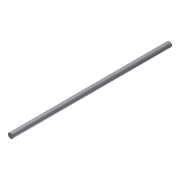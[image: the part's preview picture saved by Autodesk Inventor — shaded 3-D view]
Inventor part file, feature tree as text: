
AUTODESK INVENTOR PART (.ipt)
format: ipt  version: 2016 (Build 200138000, 138)  size: 82,432 bytes
history: native  units: in
note: dims shown in document units (in); Inventor stores cm internally (conversion verified against a paired STEP export)
features: other x1, imported_body x1, extrude x1, sketch x1
ambient origin geometry x8: Origin, YZ Plane, XZ Plane, XY Plane, X Axis, Y Axis, Z Axis, Center Point
bodies: Body1 (feature_tree)
feature tree (4):
  other  "AXLE_D-SHAFT_250_2011"
  imported_body  "Base1"
  extrude  "Extrusion1"  [1 undecoded]
  sketch  "Sketch1"  dims[d0=4.098in d1=0.0in]
note: 1 required parameter value undecoded (feature->parameter linkage not recoverable at this tier; creation-order binding heuristic only, values carry confidence <= 0.55)
